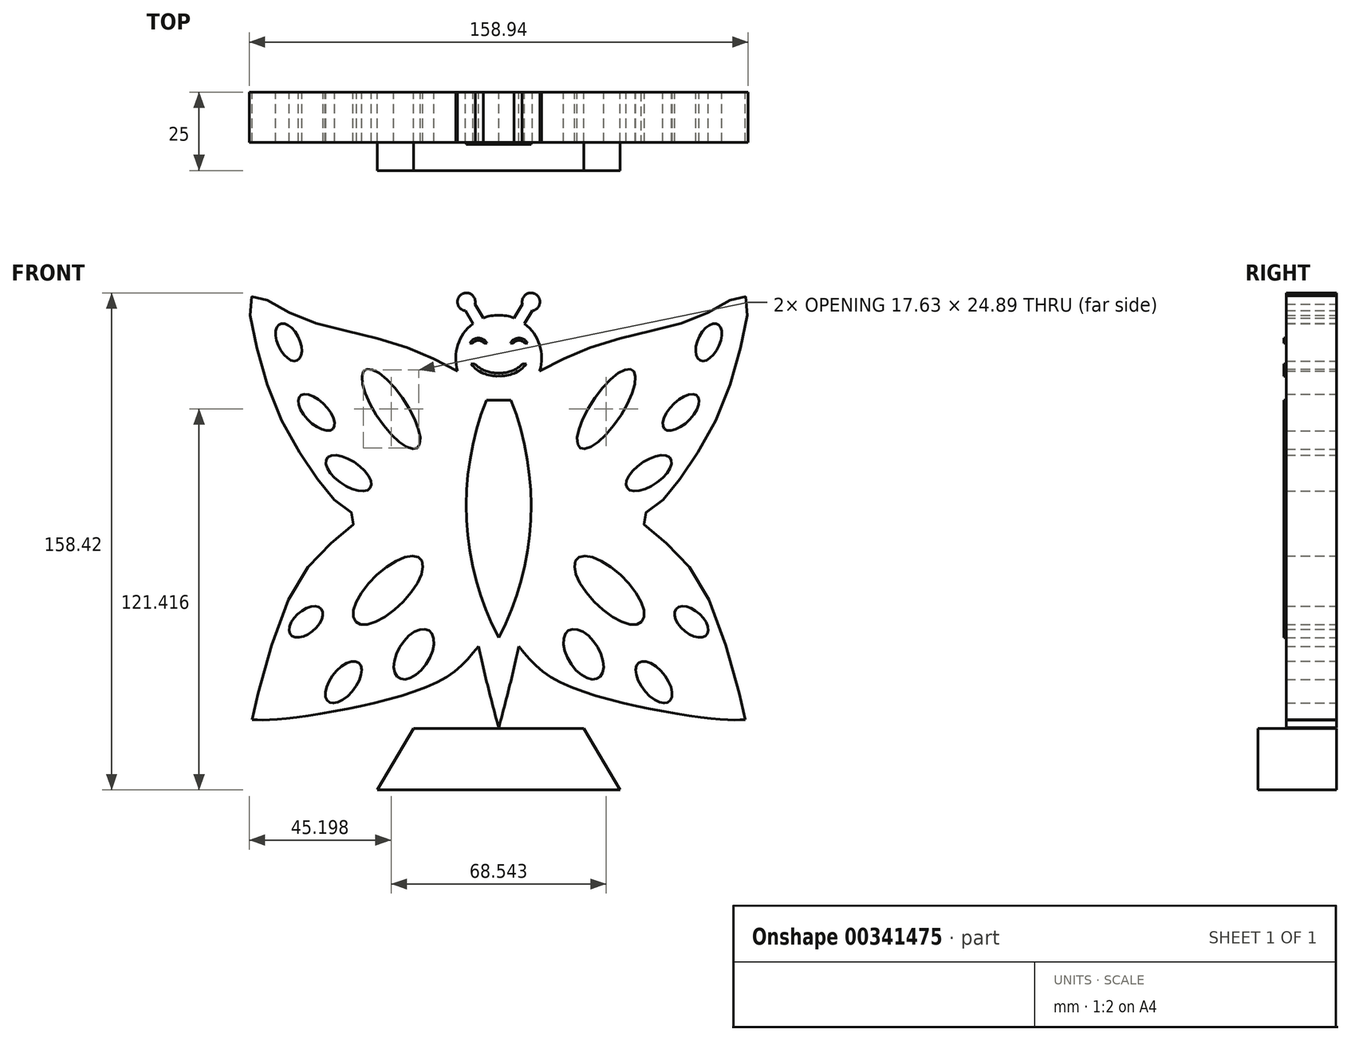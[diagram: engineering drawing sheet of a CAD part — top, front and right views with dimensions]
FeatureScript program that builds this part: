
annotation { "Feature Type Name" : "Feature", "Feature Type Description" : "" }
export const myFeature = defineFeature(function(context is Context, id is Id, definition is map)
    precondition{}
    {
        {
            var Q0;
            Q0=qCreatedBy(makeId("Front.planeOp"),FACE);
            var sketch = newSketch(context, id + "F0", { "sketchPlane" : qUnion([Q0])});
            skPoint(sketch, "E0.center.orphan", {"position": v(0, 42.5) * mm});
            skPoint(sketch, "E1.center.orphan", {"position": v(0, 56.68) * mm});
            skArc(sketch, "E2", {"start": v(-8.23, 58.63) * mm, "mid": v(-13.48, 45.22) * mm, "end": v(-3.84, 34.53) * mm});
            skFitSpline(sketch, "E3", {"points": [v(-3.84, 34.53) * mm, v(-10.48, -14.17) * mm, v(0, -70.17) * mm], "startDerivative": vector(-22, -99.5) * mm, "endDerivative": vector(29.04, -109.8) * mm});
            skFitSpline(sketch, "E4", {"points": [v(-13.08, 43.6) * mm, v(-26.53, 50) * mm, v(-45.06, 55.53) * mm, v(-63.04, 60.5) * mm, v(-74.65, 66.6) * mm, v(-78.8, 67.15) * mm, v(-78.25, 56.36) * mm, v(-69.95, 29.53) * mm, v(-57.78, 9.34) * mm, v(-49.46, 0) * mm, v(-45.34, -3.39) * mm, v(-54.46, -12.24) * mm, v(-69.4, -35.2) * mm, v(-78.53, -67.56) * mm, v(-78.53, -67.83) * mm], "startDerivative": vector(-174.1, 91.02) * mm, "endDerivative": vector(3.2, -14.45) * mm});
            skFitSpline(sketch, "E5", {"points": [v(-78.53, -67.56) * mm, v(-71.89, -67.56) * mm, v(-47.55, -63.96) * mm, v(-17.12, -54.28) * mm, v(-6.46, -44.2) * mm], "startDerivative": vector(37.48, -1.73) * mm, "endDerivative": vector(38.3, 47.43) * mm});
            skFitSpline(sketch, "E6.MirrorCS", {"points": [v(13.08, 43.6) * mm, v(26.53, 50) * mm, v(45.06, 55.53) * mm, v(63.04, 60.5) * mm, v(74.65, 66.6) * mm, v(78.8, 67.15) * mm, v(78.25, 56.36) * mm, v(69.95, 29.53) * mm, v(57.78, 9.34) * mm, v(49.46, 0) * mm, v(45.34, -3.39) * mm, v(54.46, -12.24) * mm, v(69.4, -35.2) * mm, v(78.53, -67.56) * mm, v(78.53, -67.83) * mm], "startDerivative": vector(174.1, 91.02) * mm, "endDerivative": vector(-3.2, -14.45) * mm});
            skFitSpline(sketch, "E7.MirrorCS", {"points": [v(78.53, -67.56) * mm, v(71.89, -67.56) * mm, v(47.55, -63.96) * mm, v(17.12, -54.28) * mm, v(6.46, -44.2) * mm], "startDerivative": vector(-37.48, -1.73) * mm, "endDerivative": vector(-38.3, 47.43) * mm});
            skFitSpline(sketch, "E8.MirrorCS", {"points": [v(3.84, 34.53) * mm, v(10.48, -14.17) * mm, v(0, -70.17) * mm], "startDerivative": vector(22, -99.5) * mm, "endDerivative": vector(-29.04, -109.8) * mm});
            skEllipse(sketch, "E9", {"center": v(-34.27, 31.47) * mm, "majorRadius": 14.96 * mm, "minorRadius": 5 * mm, "majorAxis": v(0.55, -0.83)});
            skEllipse(sketch, "E10", {"center": v(-66.9, 52.76) * mm, "majorRadius": 6.43 * mm, "minorRadius": 3.46 * mm, "majorAxis": v(0.43, -0.9)});
            skEllipse(sketch, "E11", {"center": v(-58.06, 30.36) * mm, "majorRadius": 7.43 * mm, "minorRadius": 3.54 * mm, "majorAxis": v(0.7, -0.7)});
            skEllipse(sketch, "E12", {"center": v(-47.82, 11) * mm, "majorRadius": 8.36 * mm, "minorRadius": 3.95 * mm, "majorAxis": v(0.83, -0.56)});
            skLineSegment(sketch, "E13", {"start": v(-8.23, 58.63) * mm, "end": v(-10.67, 62.8) * mm});
            skLineSegment(sketch, "E14", {"start": v(-4.86, 60.49) * mm, "end": v(-7.56, 64.85) * mm});
            skArc(sketch, "E15", {"start": v(-7.56, 64.85) * mm, "mid": v(-11.87, 68) * mm, "end": v(-10.67, 62.8) * mm});
            skPoint(sketch, "E16.orphan", {"position": v(-12.37, 65.72) * mm});
            skPoint(sketch, "E17.orphan", {"position": v(-8.1, 65.72) * mm});
            skLineSegment(sketch, "E18.MirrorCS", {"start": v(4.86, 60.49) * mm, "end": v(7.56, 64.85) * mm});
            skArc(sketch, "E19.MirrorCS", {"start": v(7.56, 64.85) * mm, "mid": v(11.87, 68) * mm, "end": v(10.67, 62.8) * mm});
            skLineSegment(sketch, "E20.MirrorCS", {"start": v(8.23, 58.63) * mm, "end": v(10.67, 62.8) * mm});
            skEllipse(sketch, "E21.MirrorC", {"center": v(34.27, 31.47) * mm, "majorRadius": 14.96 * mm, "minorRadius": 5 * mm, "majorAxis": v(-0.55, -0.83)});
            skEllipse(sketch, "E22.MirrorC", {"center": v(58.06, 30.36) * mm, "majorRadius": 7.43 * mm, "minorRadius": 3.54 * mm, "majorAxis": v(-0.7, -0.7)});
            skEllipse(sketch, "E23.MirrorC", {"center": v(66.9, 52.76) * mm, "majorRadius": 6.43 * mm, "minorRadius": 3.46 * mm, "majorAxis": v(-0.43, -0.9)});
            skEllipse(sketch, "E24.MirrorC", {"center": v(47.82, 11) * mm, "majorRadius": 8.36 * mm, "minorRadius": 3.95 * mm, "majorAxis": v(-0.83, -0.56)});
            skEllipse(sketch, "E25", {"center": v(-35.27, -26.33) * mm, "majorRadius": 14.4 * mm, "minorRadius": 6 * mm, "majorAxis": v(-0.72, -0.7)});
            skEllipse(sketch, "E26", {"center": v(-61.36, -36.4) * mm, "majorRadius": 6.33 * mm, "minorRadius": 3.65 * mm, "majorAxis": v(0.76, 0.65)});
            skEllipse(sketch, "E27", {"center": v(-49.46, -55.63) * mm, "majorRadius": 7.86 * mm, "minorRadius": 4.05 * mm, "majorAxis": v(0.62, 0.79)});
            skEllipse(sketch, "E28", {"center": v(-27.02, -46.7) * mm, "majorRadius": 8.95 * mm, "minorRadius": 5.03 * mm, "majorAxis": v(0.54, 0.84)});
            skEllipse(sketch, "E29.MirrorC", {"center": v(35.27, -26.33) * mm, "majorRadius": 14.4 * mm, "minorRadius": 6 * mm, "majorAxis": v(0.72, -0.7)});
            skEllipse(sketch, "E30.MirrorC", {"center": v(27.02, -46.7) * mm, "majorRadius": 8.95 * mm, "minorRadius": 5.03 * mm, "majorAxis": v(-0.54, 0.84)});
            skEllipse(sketch, "E31.MirrorC", {"center": v(61.36, -36.4) * mm, "majorRadius": 6.33 * mm, "minorRadius": 3.65 * mm, "majorAxis": v(-0.76, 0.65)});
            skEllipse(sketch, "E32.MirrorC", {"center": v(49.46, -55.63) * mm, "majorRadius": 7.86 * mm, "minorRadius": 4.05 * mm, "majorAxis": v(-0.62, 0.79)});
            skArc(sketch, "E33.trimOffspring", {"start": v(3.84, 34.53) * mm, "mid": v(13.48, 45.22) * mm, "end": v(8.23, 58.63) * mm});
            skArc(sketch, "E34.trimOffspring", {"start": v(4.86, 60.49) * mm, "mid": v(0, 61.38) * mm, "end": v(-4.86, 60.49) * mm});
            skSolve(sketch);
        }
        {
            var Q0;
            {var subQ7=sQuery(id+"F0.wireOp",EDGE,"E13");Q0=makeQuery(id+"F0.imprint","IMPRINT",FACE,{"disambiguationData":[TD([[makeQuery(id+"F0.imprint","IMPRINT",EDGE,{"derivedFrom":subQ7}),-1.0]])]});}
            var Q1;
            {var subQ3=sQuery(id+"F0.wireOp",EDGE,"E7.MirrorCS");Q1=makeQuery(id+"F0.imprint","IMPRINT",FACE,{"disambiguationData":[TD([[makeQuery(id+"F0.imprint","IMPRINT",EDGE,{"derivedFrom":subQ3}),-1.0]])]});}
            var Q2;
            {var subQ3=sQuery(id+"F0.wireOp",EDGE,"E5");Q2=makeQuery(id+"F0.imprint","IMPRINT",FACE,{"disambiguationData":[TD([[makeQuery(id+"F0.imprint","IMPRINT",EDGE,{"derivedFrom":subQ3}),1.0]])]});}
            extrude(context, id + "F1", {"entities" : qUnion([Q0, Q1, Q2]), "depth" : 16 * mm});
        }
        {
            var Q0;
            Q0=qCreatedBy(makeId("Front.planeOp"),FACE);
            var sketch = newSketch(context, id + "F2", { "sketchPlane" : qUnion([Q0])});
            skLineSegment(sketch, "E35", {"start": v(0, -70.32) * mm, "end": v(-27.14, -70.32) * mm});
            skLineSegment(sketch, "E36", {"start": v(-27.14, -70.32) * mm, "end": v(-38.7, -89.95) * mm});
            skLineSegment(sketch, "E37", {"start": v(-38.7, -89.95) * mm, "end": v(0, -89.95) * mm});
            skPoint(sketch, "E38.MirrorCS.end.orphan", {"position": v(-38.7, -50.7) * mm});
            skPoint(sketch, "E38.MirrorCS.start.orphan", {"position": v(-27.14, -70.32) * mm});
            skLineSegment(sketch, "E39.MirrorCS", {"start": v(0, -70.32) * mm, "end": v(27.14, -70.32) * mm});
            skLineSegment(sketch, "E40.MirrorCS", {"start": v(27.14, -70.32) * mm, "end": v(38.7, -89.95) * mm});
            skLineSegment(sketch, "E41.MirrorCS", {"start": v(38.7, -89.95) * mm, "end": v(0, -89.95) * mm});
            skSolve(sketch);
        }
        {
            var Q0;
            Q0 = qSketchRegion(id + "F2", true);
            extrude(context, id + "F3", {"entities" : qUnion([Q0]), "depth" : 25 * mm});
        }
        {
            var Q0;
            Q0=qCreatedBy(makeId("Front.planeOp"),FACE);
            var sketch = newSketch(context, id + "F4", { "sketchPlane" : qUnion([Q0])});
            skArc(sketch, "E42", {"start": v(-3.76, 52.47) * mm, "mid": v(-6.48, 54.08) * mm, "end": v(-9.17, 52.43) * mm});
            skLineSegment(sketch, "E43", {"start": v(-9.17, 52.43) * mm, "end": v(-8.3, 52.43) * mm});
            skArc(sketch, "E44", {"start": v(-4.66, 52.43) * mm, "mid": v(-6.48, 53.3) * mm, "end": v(-8.3, 52.43) * mm});
            skLineSegment(sketch, "E45", {"start": v(-4.66, 52.43) * mm, "end": v(-3.76, 52.47) * mm});
            skArc(sketch, "E46.MirrorCS", {"start": v(3.76, 52.47) * mm, "mid": v(6.48, 54.08) * mm, "end": v(9.17, 52.43) * mm});
            skArc(sketch, "E47.MirrorCS", {"start": v(4.66, 52.43) * mm, "mid": v(6.48, 53.3) * mm, "end": v(8.3, 52.43) * mm});
            skLineSegment(sketch, "E48.MirrorCS", {"start": v(4.66, 52.43) * mm, "end": v(3.76, 52.47) * mm});
            skLineSegment(sketch, "E49.MirrorCS", {"start": v(9.17, 52.43) * mm, "end": v(8.3, 52.43) * mm});
            skArc(sketch, "E50", {"start": v(-8.81, 45.87) * mm, "mid": v(-4.89, 42.83) * mm, "end": v(0, 41.96) * mm});
            skLineSegment(sketch, "E51", {"start": v(-8.81, 45.87) * mm, "end": v(-7.62, 45.87) * mm});
            skFitSpline(sketch, "E52", {"points": [v(-7.62, 45.87) * mm, v(-5.04, 43.92) * mm, v(-1.32, 42.97) * mm, v(0, 42.97) * mm], "startDerivative": vector(6.15, -5.9) * mm, "endDerivative": vector(4.78, 0.32) * mm});
            skFitSpline(sketch, "E53.MirrorCS", {"points": [v(7.62, 45.87) * mm, v(5.04, 43.92) * mm, v(1.32, 42.97) * mm, v(0, 42.97) * mm], "startDerivative": vector(-6.15, -5.9) * mm, "endDerivative": vector(-4.78, 0.32) * mm});
            skLineSegment(sketch, "E54.MirrorCS", {"start": v(8.81, 45.87) * mm, "end": v(7.62, 45.87) * mm});
            skArc(sketch, "E55.MirrorCS", {"start": v(8.81, 45.87) * mm, "mid": v(4.89, 42.83) * mm, "end": v(0, 41.96) * mm});
            skArc(sketch, "E56", {"start": v(-3.94, 34.3) * mm, "mid": v(-10.18, -3.96) * mm, "end": v(0, -41.36) * mm});
            skArc(sketch, "E57.MirrorCS", {"start": v(3.94, 34.3) * mm, "mid": v(10.18, -3.96) * mm, "end": v(0, -41.36) * mm});
            skLineSegment(sketch, "E58", {"start": v(-3.94, 34.3) * mm, "end": v(3.94, 34.3) * mm});
            skLineSegment(sketch, "E59", {"start": v(0, 29.13) * mm, "end": v(0, -28.01) * mm});
            skSolve(sketch);
        }
        {
            var Q0;
            Q0 = qSketchRegion(id + "F4", true);
            extrude(context, id + "F5", {"entities" : qUnion([Q0]), "operationType" : NewBodyOperationType.ADD, "depth" : 16.7 * mm});
        }
    });
